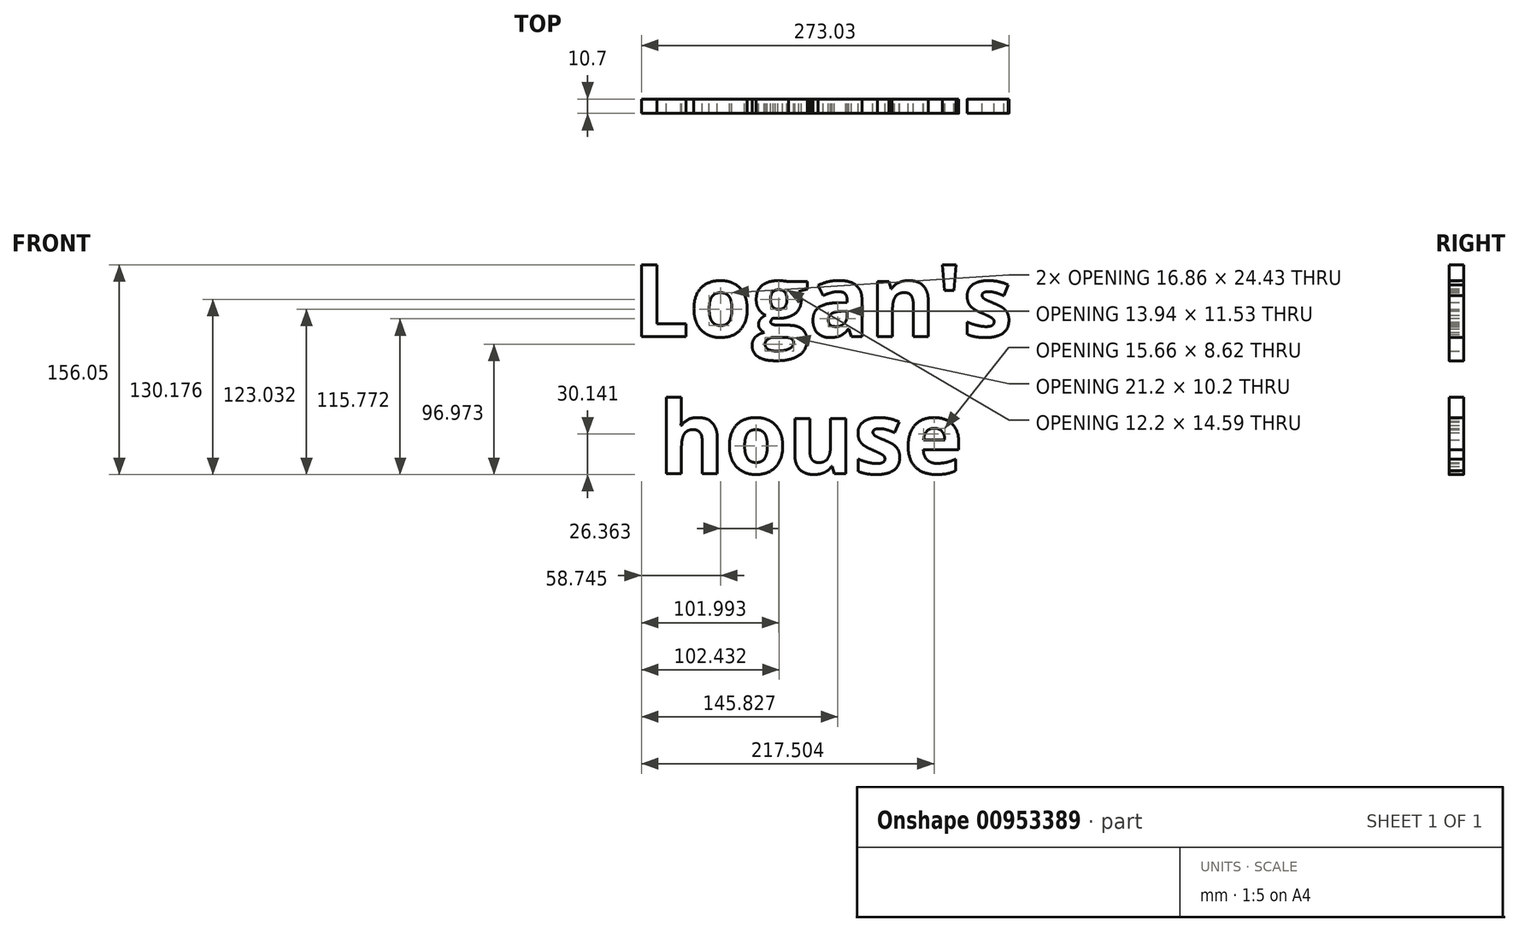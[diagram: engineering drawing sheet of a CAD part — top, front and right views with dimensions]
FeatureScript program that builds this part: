
annotation { "Feature Type Name" : "Feature", "Feature Type Description" : "" }
export const myFeature = defineFeature(function(context is Context, id is Id, definition is map)
    precondition{}
    {
        {
            var Q0;
            Q0=qCreatedBy(makeId("Front.planeOp"),FACE);
            var sketch = newSketch(context, id + "F0", { "sketchPlane" : qUnion([Q0])});
            skText(sketch, "E0", { "text": "Logan\'s\n house", "fontName": "OpenSans-Bold.ttf"});
            const initialGuessF0  = {"E0": [-0.07028, 0.01736, 1, 0, 0.05392]};
            skSetInitialGuess(sketch, initialGuessF0);
            skSolve(sketch);
        }
        {
            var Q0;
            Q0 = qSketchRegion(id + "F0", true);
            extrude(context, id + "F1", {"entities" : qUnion([Q0]), "depth" : 10.7 * mm, "offsetDistance" : 25 * mm});
        }
    });
